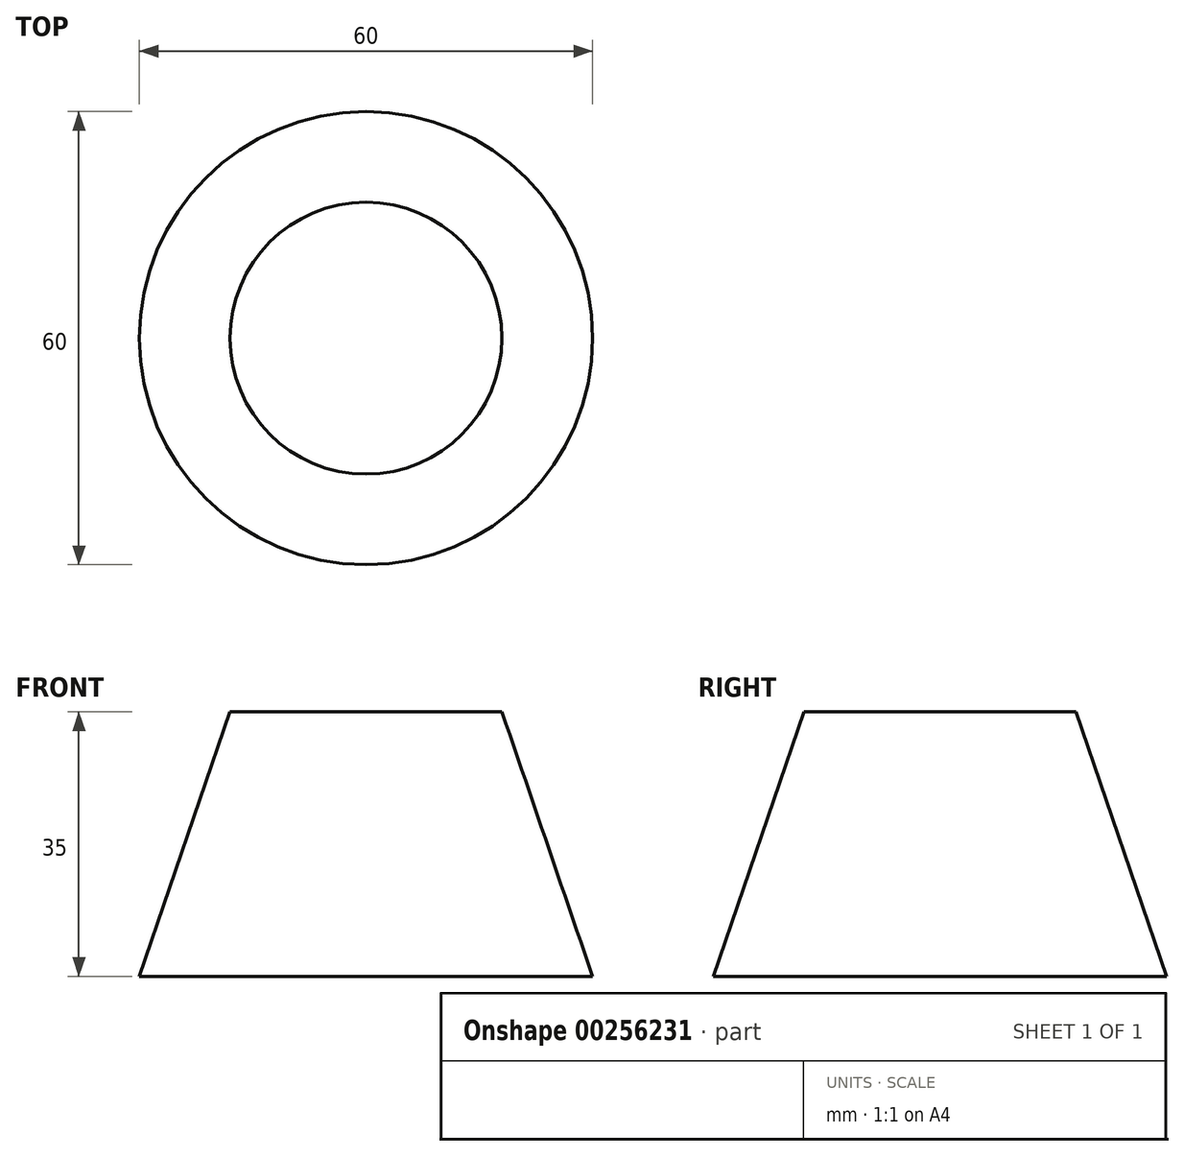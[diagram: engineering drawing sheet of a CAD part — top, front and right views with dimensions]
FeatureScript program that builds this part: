
annotation { "Feature Type Name" : "Feature", "Feature Type Description" : "" }
export const myFeature = defineFeature(function(context is Context, id is Id, definition is map)
    precondition{}
    {
        {
            var Q0;
            Q0=qCreatedBy(makeId("Front.planeOp"),FACE);
            var sketch = newSketch(context, id + "F0", { "sketchPlane" : qUnion([Q0])});
            skLineSegment(sketch, "E0", {"start": v(0, 0) * mm, "end": v(0, 35) * mm});
            skLineSegment(sketch, "E1", {"start": v(0, 35) * mm, "end": v(18, 35) * mm});
            skLineSegment(sketch, "E2", {"start": v(18, 35) * mm, "end": v(30, 0) * mm});
            skLineSegment(sketch, "E3", {"start": v(30, 0) * mm, "end": v(0, 0) * mm});
            skLineSegment(sketch, "E4", {"start": v(0, 52.72) * mm, "end": v(0, -41.83) * mm, "construction": true});
            skPoint(sketch, "E4.startSnap0", {"position": v(0, 17.5) * mm});
            skSolve(sketch);
        }
        {
            var Q0;
            Q0=makeQuery(id+"F0.imprint","IMPRINT",FACE,{"disambiguationData":[TD([[makeQuery(id+"F0.imprint","IMPRINT",EDGE,{"derivedFrom":sQuery(id+"F0.wireOp",EDGE,"E0")}),-1.0]])]});
            var Q1;
            Q1=sQuery(id+"F0.wireOp",EDGE,"E4");
            revolve(context, id + "F1", {"entities" : qUnion([Q0]), "axis" : qUnion([Q1]), "revolveType" : RevolveType.FULL});
        }
    });
